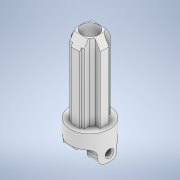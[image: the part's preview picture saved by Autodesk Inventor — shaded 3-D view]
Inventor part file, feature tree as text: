
AUTODESK INVENTOR PART (.ipt)
format: ipt  version: 2022 (Build 260153000, 153)  size: 317,952 bytes
history: native  units: in
note: dims shown in document units (in); Inventor stores cm internally (conversion verified against a paired STEP export)
features: sketch x7, extrude x6, chamfer x2, pattern_circular x1, fillet x1, hole x1
ambient origin geometry x8: Origin, YZ Plane, XZ Plane, XY Plane, X Axis, Y Axis, Z Axis, Center Point
bodies: Solid1 (feature_tree)
feature tree (18):
  extrude  "Extrusion1"  Depth=0.1969in TaperAngle=0.0deg
  extrude  "Extrusion2"  Depth=0.2756in TaperAngle=0.0deg
  extrude  "Extrusion3"  Depth=1.5748in TaperAngle=360.0deg
  extrude  "Extrusion4"  Depth=0.2717in
  extrude  "Extrusion5"  Depth=0.7874in TaperAngle=360.0deg
  pattern_circular  "Circular Pattern1"  [2 undecoded]
  fillet  "Fillet2"  Radius=0.1358in
  hole  "Hole2"  [1 undecoded]
  chamfer  "Chamfer2"  Distance=0.0197in Angle=45.0deg
  chamfer  "Chamfer3"  Distance=0.2953in
  extrude  "Extrusion6"  Depth=0.122in
  sketch  "Sketch1"  dims[d0=0.5512in d2=0.1969in d3=0.0in]
  sketch  "Sketch2"  dims[d13=1.063in d14=0.0in d17=0.2756in d18=0.0in]
  sketch  "Sketch3"  dims[d26=0.0787in d27=1.5748in d29=360.0deg]
  sketch  "Sketch4"  dims[d31=0.0787in d32=0.0in d33=0.2717in]
  sketch  "Sketch5"  dims[d34=0.1969in d35=0.0in d47=0.7874in d48=360.0deg]
  sketch  "Sketch7"  dims[d50=0.1772in]
  sketch  "Sketch9"  dims[d51=0.0787in d52=0.0984in d53=0.1358in d54=0.0787in d55=0.2362in d56=0.1575in d57=0.0787in d58=90.0deg d59=0.315in d60=0.8108in d61=0.2362in d62=0.0197in d63=0.0787in d64=45.0deg d65=0.2953in d67=0.122in d68=0.1102in d69=1.5748in d71=360.0deg d75=0.2008in d76=0.0236in d78=0.7874in d80=360.0deg d82=0.0787in d83=0.0787in d84=60.0deg d85=0.1969in d86=0.0in d88=0.1004in d90=0.0925in]
note: 3 required parameter values undecoded (feature->parameter linkage not recoverable at this tier; creation-order binding heuristic only, values carry confidence <= 0.55)
